# Revit family: TYCO-FPP-FireClass-FC410QMO QUAD MONITORED OP
name_source: partatom
category: Electrical Fixtures
revit_build: Autodesk Revit 2014 (Build: 20130308_1515(x64)
units: mm (PartAtom-declared; Revit-internal decimal feet)

## types (1)
- TYCO-FPP-FireClass-FC410QMO QUAD MONITORED OP
    Approvals = EN54-17 and EN54-18
    Description = Quad Output Unit
    EOLResistor Value = 27k Ohm
    Keynote = to the MZX Digital loop and requires a 24Vdc or 48Vdc
power supply.
    Length = 103 mm
    Manufacturer = Tyco
    Model = FireClass -555.800.770
    Operating Humidity = Up to 95 %
    Operating Temperature = -25 to +70 oC
    PCB = PCB
    RS = RS
    RSS = res
    ST = ST12
    Storage Temparature = 40 to +80 oC
    Type Comments = The FC410QMO comprises of four monitored relay outputs
that are suitable for 24Vdc sounders.
    URL = https://fireclass.co.uk
    Width = 134 mm

## geometry (parser evidence)
native form markers: Sweep x1
no freeform markers — native parametric forms only
